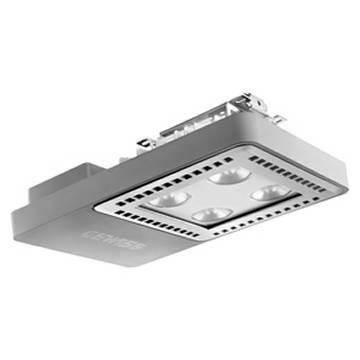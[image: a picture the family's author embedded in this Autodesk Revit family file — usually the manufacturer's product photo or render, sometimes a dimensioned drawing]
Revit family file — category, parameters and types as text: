
# Revit family: Lighting-Industrial-GEWISS-SMART[4]HE_HIGHBAYS-LED_1M_DALI
name_source: partatom
category: Apparecchi per illuminazione
units: mm (PartAtom-declared; Revit-internal decimal feet)

## family parameters
Basato su piano di lavoro = Sì
Condiviso = No
Numero OmniClass = 23.80.00.00
Punto di calcolo locali = Sì
Quota connettore circolare = Usa diametro
Sempre verticale = No
Sorgente d'illuminazione = No
Taglio con vuoti quando caricato = No
Tipo di parte = Normale
Titolo OmniClass = Electric Power and Lighting

## types (36) — shared parameters
Application = Internal
Body = PA6 "Halogen Free" loaded fibreglass
Carico apparente = 50 VA
Catalogue = LIGHTING
Classification: = -
Classificazione = Lighting
Color Rendering Index = CRI-80
Colour = Grey RAL 7035
Colour : = Grey RAL 7035
Commenti sul wattaggio = 50W
Context = Logistics and industrial manufacturing lighting
Control System = 1 x DALI DT6
Control System : = DALI
DIN 18032-3 certification = With Bracket - Rope Kit + terminal(in approval)
Device with reduced surface temperature = Yes
Distanza tot_plafoniera = 74 mm  [stored 0.242782 ft]
Driver = Included
Driver Box = Built-in
Electrocod = 2444
Eletrical and lighting features = -
External screw = Stainless steel
Fixing = -
Gasket = anti-aging silicone
General information = -
Glow Wire Test : = 850 °C
IDF = 27a589e5-b0d0-4267-8400-54dfcb229af4
IDT = 9d21ab41a4404c819d8f88b838f402fb
IP degree = IP66
IPEA = -
Immagine tipo = GWL1071.jpg
Installationa and maintenance = -
Insulation class = I
LED Maintenance = Non-replaceable
Lampada = LED
Larghezza = 253 mm  [stored 0.830052 ft]
Lifetime = L90B10 (Tq+25°C) = 100.000 h - L90B10 (Tq+50°C) = 50.000 h
Locking Hook = -
Luminaire = LED Industrial ReflectorÂ
Lunghezza = 383 mm  [stored 1.25656 ft]
Materials = -
Maximum surface exposed to the wind : = 0,097 m²
Motore = <Per categoria>
Mouting and installation = Ceiling - Wallmounting - Suspension
Operating temperature : = -30°C ÷ +50 °C
Optic Maintenance = Non-replaceable
Optic and illuminating features = -
Overvoltage protection = DM 6 kV / CM 10 kV
Photobiological Risk Class = RG0
Plafoniera = <Per categoria>
Produttore = GEWISS S.p.A.
Prospetto di default = 1219 mm
Raggio led = 30 mm  [stored 0.0984252 ft]
Rated frequency (Hz) = 50/60 Hz
Shield type = Tempered glass Thickness 4mm
Shock resistance = IK08
Spessore plafoniera = 40 mm  [stored 0.131234 ft]
Standard Deviation Colour Matching = SDCM = 3
Standard- = EN 60598-1 ; EN 60598-2-1 ; EN 60598-2-24
Standards and approvals = -
Stocking temperature = -40 +70 °C
Supply voltage = 220 - 240 V
System power = 48W
Technical sheet = https://www.gewiss.com
Tilt- = With bracket accessory
Trasformatore = <Per categoria>
Type of light source = LED - Not replaceable
URL = https://www.gewiss.com
Unique digital code (Datamatrix) = Datamatrix
Version file RFA = 20.11
Vetro acceso = Lampada accesa
Voltaggio = 230 V
Warranty = 5 years
Weight (kg): = 3,5
Wiring = With GW connect watertight connector

## per-type parameters (varying)
| type | Colour temperature | Descrizione | Efficiency (lm/W) | Lumen output (lm) | Modello | Optic | Optic : | SEO | Unified Glare Rating |
| GWS4123AP840 - SMART4LB 1M C.PAS.DALI 90° 40K | 4000K | SMART[4]LB 1M C.PAS.DALI 90° 40K | 150 | 7200 | GWS4123AP840 | 90° | Metallic PC reflector and PMMA lenses |  | UGR - 25 |
| GWS4121AC830 - SMART4LB 1M ST.AL.DALI ASI.30K | 3000K | SMART[4]LB 1M ST.AL.DALI ASI.30K | 125 | 6000 | GWS4121AC830 | Asymmetrical | Metallic PC reflector and PMMA lenses | Low bay | - |
| GWS4123AA840 - SMART4LB 1M C.PAS.DALI ARR.40K | 4000K | SMART[4]LB 1M C.PAS.DALI ARR.40K | 148 | 7100 | GWS4123AA840 | Array | Metallized polycarbonate reflector |  | - |
| GWS4121AP840 - SMART4LB 1M ST.AL.DALI 90° 40K | 4000K | SMART[4]LB 1M ST.AL.DALI 90° 40K | 150 | 7200 | GWS4121AP840 | 90° | Metallic PC reflector and PMMA lenses |  | UGR - 25 |
| GWS4121AQ830 - SMART4LB 1M ST.AL.DALI ELL.30K | 3000K | SMART[4]LB 1M ST.AL.DALI ELL.30K | 125 | 6000 | GWS4121AQ830 | Elliptical | Metallic PC reflector and PMMA lenses | Low bay | - |
| GWS4123AP830 - SMART4LB 1M C.PAS.DALI 90° 30K | 3000K | SMART[4]LB 1M C.PAS.DALI 90° 30K | 142 | 6800 | GWS4123AP830 | 90° | Metallic PC reflector and PMMA lenses |  | UGR - 25 |
| GWS4123AP857 - SMART4LB 1M C.PAS.DALI 90° 57K | 5700K | SMART[4]LB 1M C.PAS.DALI 90° 57K | 150 | 7200 | GWS4123AP857 | 90° | Metallic PC reflector and PMMA lenses |  | UGR - 25 |
| GWS4123AQ840 - SMART4LB 1M C.PAS.DALI ELL.40K | 4000K | SMART[4]LB 1M C.PAS.DALI ELL.40K | 131 | 6300 | GWS4123AQ840 | Elliptical | Metallic PC reflector and PMMA lenses | Low bay | - |
| GWS4121AF857 - SMART4LB 1M ST.AL.DALI 30° 57K | 5700K | SMART[4]LB 1M ST.AL.DALI 30° 57K | 146 | 7000 | GWS4121AF857 | 30° | Metallic PC reflector and PMMA lenses |  | UGR - 22 |
| GWS4121AH857 - SMART4LB 1M ST.AL.DALI 60° 57K | 5700K | SMART[4]LB 1M ST.AL.DALI 60° 57K | 146 | 7000 | GWS4121AH857 | 60° | Metallic PC reflector and PMMA lenses |  | UGR - 22 |
| GWS4121AC857 - SMART4LB 1M ST.AL.DALI ASI.57K | 5700K | SMART[4]LB 1M ST.AL.DALI ASI.57K | 131 | 6300 | GWS4121AC857 | Asymmetrical | Metallic PC reflector and PMMA lenses | Low bay | - |
| GWS4121AP857 - SMART4LB 1M ST.AL.DALI 90° 57K | 5700K | SMART[4]LB 1M ST.AL.DALI 90° 57K | 150 | 7200 | GWS4121AP857 | 90° | Metallic PC reflector and PMMA lenses |  | UGR - 25 |
| GWS4123AH857 - SMART4LB 1M C.PAS.DALI 60° 57K | 5700K | SMART[4]LB 1M C.PAS.DALI 60° 57K | 146 | 7000 | GWS4123AH857 | 60° | Metallic PC reflector and PMMA lenses |  | UGR - 22 |
| GWS4123AQ830 - SMART4LB 1M C.PAS.DALI ELL.30K | 3000K | SMART[4]LB 1M C.PAS.DALI ELL.30K | 125 | 6000 | GWS4123AQ830 | Elliptical | Metallic PC reflector and PMMA lenses | Low bay | - |
| GWS4121AF840 - SMART4LB 1M ST.AL.DALI 30° 40K | 4000K | SMART[4]LB 1M ST.AL.DALI 30° 40K | 146 | 7000 | GWS4121AF840 | 30° | Metallic PC reflector and PMMA lenses |  | UGR - 22 |
| GWS4121AH840 - SMART4LB 1M ST.AL.DALI 60° 40K | 4000K | SMART[4]LB 1M ST.AL.DALI 60° 40K | 146 | 7000 | GWS4121AH840 | 60° | Metallic PC reflector and PMMA lenses |  | UGR - 22 |
| GWS4121AC840 - SMART4LB 1M ST.AL.DALI ASI.40K | 4000K | SMART[4]LB 1M ST.AL.DALI ASI.40K | 131 | 6300 | GWS4121AC840 | Asymmetrical | Metallic PC reflector and PMMA lenses | Low bay | - |
| GWS4123AH840 - SMART4LB 1M C.PAS.DALI 60° 40K | 4000K | SMART[4]LB 1M C.PAS.DALI 60° 40K | 146 | 7000 | GWS4123AH840 | 60° | Metallic PC reflector and PMMA lenses |  | UGR - 22 |
| GWS4123AH830 - SMART4LB 1M C.PAS.DALI 60° 30K | 3000K | SMART[4]LB 1M C.PAS.DALI 60° 30K | 140 | 6700 | GWS4123AH830 | 60° | Metallic PC reflector and PMMA lenses |  | UGR - 22 |
| GWS4123AF830 - SMART4LB 1M C.PAS.DALI 30° 30K | 3000K | SMART[4]LB 1M C.PAS.DALI 30° 30K | 138 | 6600 | GWS4123AF830 | 30° | Metallic PC reflector and PMMA lenses |  | UGR - 22 |
| GWS4121AA857 - SMART4LB 1M ST.AL.DALI ARR.57K | 5700K | SMART[4]LB 1M ST.AL.DALI ARR.57K | 148 | 7100 | GWS4121AA857 | Array | Metallized polycarbonate reflector |  | - |
| GWS4123AQ857 - SMART4LB 1M C.PAS.DALI ELL.57K | 5700K | SMART[4]LB 1M C.PAS.DALI ELL.57K | 131 | 6300 | GWS4123AQ857 | Elliptical | Metallic PC reflector and PMMA lenses | Low bay | - |
| GWS4121AH830 - SMART4LB 1M ST.AL.DALI 60° 30K | 3000K | SMART[4]LB 1M ST.AL.DALI 60° 30K | 140 | 6700 | GWS4121AH830 | 60° | Metallic PC reflector and PMMA lenses |  | UGR - 22 |
| GWS4123AF840 - SMART4LB 1M C.PAS.DALI 30° 40K | 4000K | SMART[4]LB 1M C.PAS.DALI 30° 40K | 146 | 7000 | GWS4123AF840 | 30° | Metallic PC reflector and PMMA lenses |  | UGR - 22 |
| GWS4121AA840 - SMART4LB 1M ST.AL.DALI ARR.40K | 4000K | SMART[4]LB 1M ST.AL.DALI ARR.40K | 148 | 7100 | GWS4121AA840 | Array | Metallized polycarbonate reflector |  | - |
| GWS4123AF857 - SMART4LB 1M C.PAS.DALI 30° 57K | 5700K | SMART[4]LB 1M C.PAS.DALI 30° 57K | 146 | 7000 | GWS4123AF857 | 30° | Metallic PC reflector and PMMA lenses |  | UGR - 22 |
| GWS4123AC830 - SMART4LB 1M C.PAS.DALI ASI.30K | 3000K | SMART[4]LB 1M C.PAS.DALI ASI.30K | 125 | 6000 | GWS4123AC830 | Asymmetrical | Metallic PC reflector and PMMA lenses | Low bay | - |
| GWS4121AQ857 - SMART4LB 1M ST.AL.DALI ELL.57K | 5700K | SMART[4]LB 1M ST.AL.DALI ELL.57K | 131 | 6300 | GWS4121AQ857 | Elliptical | Metallic PC reflector and PMMA lenses | Low bay | - |
| GWS4123AC840 - SMART4LB 1M C.PAS.DALI ASI.40K | 4000K | SMART[4]LB 1M C.PAS.DALI ASI.40K | 131 | 6300 | GWS4123AC840 | Asymmetrical | Metallic PC reflector and PMMA lenses | Low bay | - |
| GWS4121AQ840 - SMART4LB 1M ST.AL.DALI ELL.40K | 4000K | SMART[4]LB 1M ST.AL.DALI ELL.40K | 131 | 6300 | GWS4121AQ840 | Elliptical | Metallic PC reflector and PMMA lenses | Low bay | - |
| GWS4123AA830 - SMART4LB 1M C.PAS.DALI ARR.30K | 3000K | SMART[4]LB 1M C.PAS.DALI ARR.30K | 140 | 6700 | GWS4123AA830 | Array | Metallized polycarbonate reflector |  | - |
| GWS4121AP830 - SMART4LB 1M ST.AL.DALI 90° 30K | 3000K | SMART[4]LB 1M ST.AL.DALI 90° 30K | 142 | 6800 | GWS4121AP830 | 90° | Metallic PC reflector and PMMA lenses |  | UGR - 25 |
| GWS4121AA830 - SMART4LB 1M ST.AL.DALI ARR.30K | 3000K | SMART[4]LB 1M ST.AL.DALI ARR.30K | 140 | 6700 | GWS4121AA830 | Array | Metallized polycarbonate reflector |  | - |
| GWS4121AF830 - SMART4LB 1M ST.AL.DALI 30° 30K | 3000K | SMART[4]LB 1M ST.AL.DALI 30° 30K | 138 | 6600 | GWS4121AF830 | 30° | Metallic PC reflector and PMMA lenses |  | UGR - 22 |
| GWS4123AC857 - SMART4LB 1M C.PAS.DALI ASI.57K | 5700K | SMART[4]LB 1M C.PAS.DALI ASI.57K | 131 | 6300 | GWS4123AC857 | Asymmetrical | Metallic PC reflector and PMMA lenses | Low bay | - |
| GWS4123AA857 - SMART4LB 1M C.PAS.DALI ARR.57K | 5700K | SMART[4]LB 1M C.PAS.DALI ARR.57K | 148 | 7100 | GWS4123AA857 | Array | Metallized polycarbonate reflector |  | - |

note: [stored X ft] marks values corroborated as IEEE doubles in the binary element streams (Revit-internal decimal feet)

## geometry (parser evidence)
native form markers: Blend x4
no freeform markers — native parametric forms only
